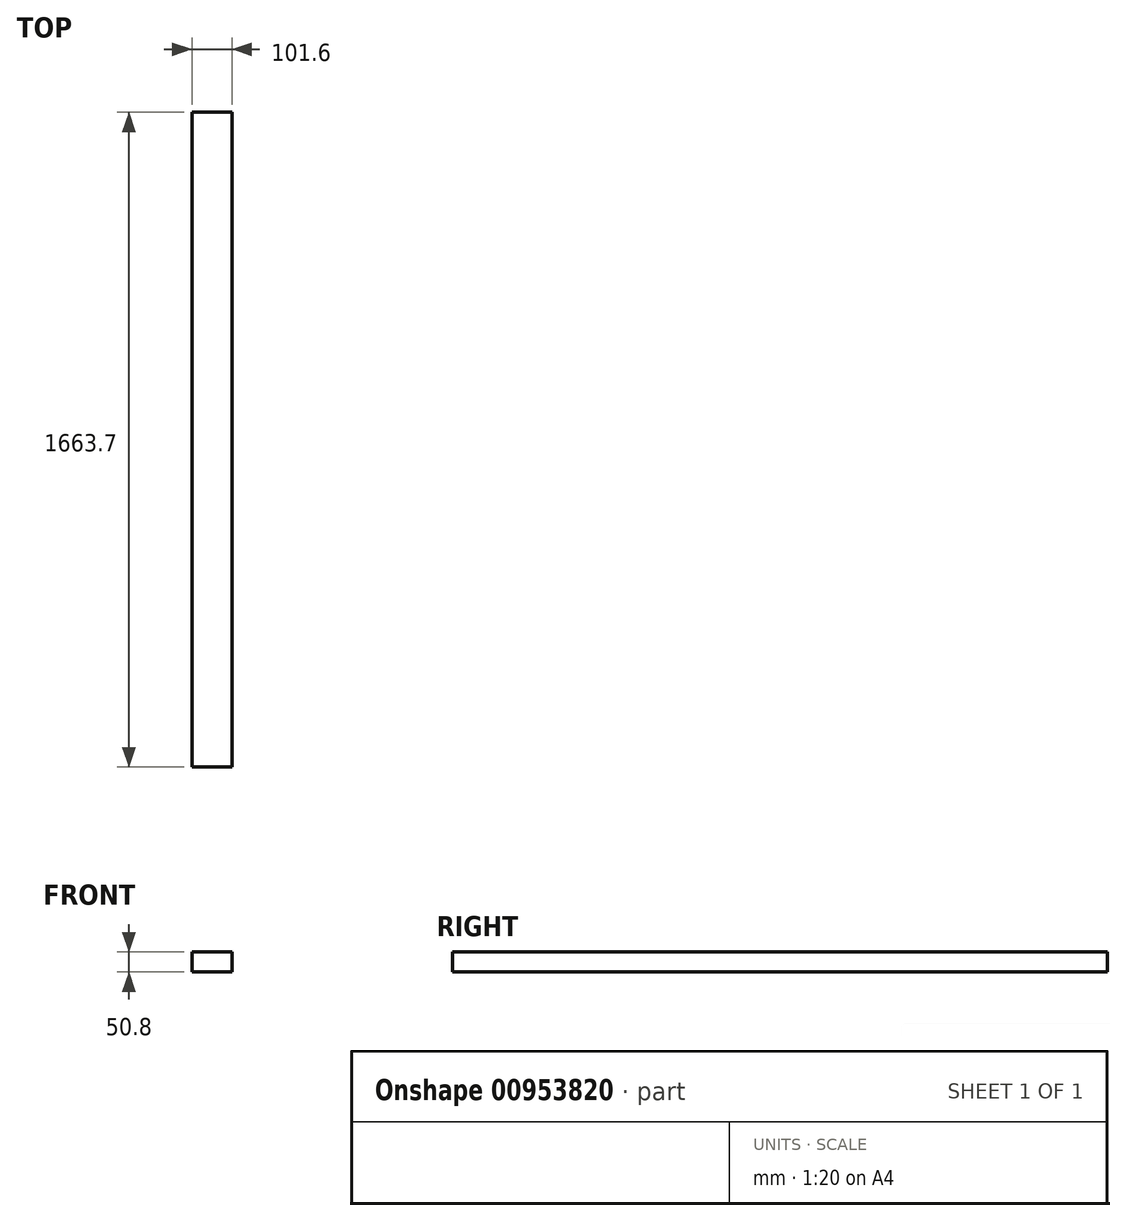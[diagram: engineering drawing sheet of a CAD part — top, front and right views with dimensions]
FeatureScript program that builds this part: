
annotation { "Feature Type Name" : "Feature", "Feature Type Description" : "" }
export const myFeature = defineFeature(function(context is Context, id is Id, definition is map)
    precondition{}
    {
        {
            var Q0;
            Q0=qCreatedBy(makeId("Front.planeOp"),FACE);
            var sketch = newSketch(context, id + "F0", { "sketchPlane" : qUnion([Q0])});
            skLineSegment(sketch, "E0.bottom", {"start": v(-50.8, -25.4) * mm, "end": v(50.8, -25.4) * mm});
            skLineSegment(sketch, "E0.top", {"start": v(-50.8, 25.4) * mm, "end": v(50.8, 25.4) * mm});
            skLineSegment(sketch, "E0.left", {"start": v(-50.8, -25.4) * mm, "end": v(-50.8, 25.4) * mm});
            skLineSegment(sketch, "E0.right", {"start": v(50.8, -25.4) * mm, "end": v(50.8, 25.4) * mm});
            skPoint(sketch, "E0.middle", {"position": v(0, 0) * mm});
            skSolve(sketch);
        }
        {
            var Q0;
            Q0 = qSketchRegion(id + "F0", true);
            extrude(context, id + "F1", {"entities" : qUnion([Q0]), "depth" : 1663.7 * mm, "offsetDistance" : 25.4 * mm});
        }
    });
